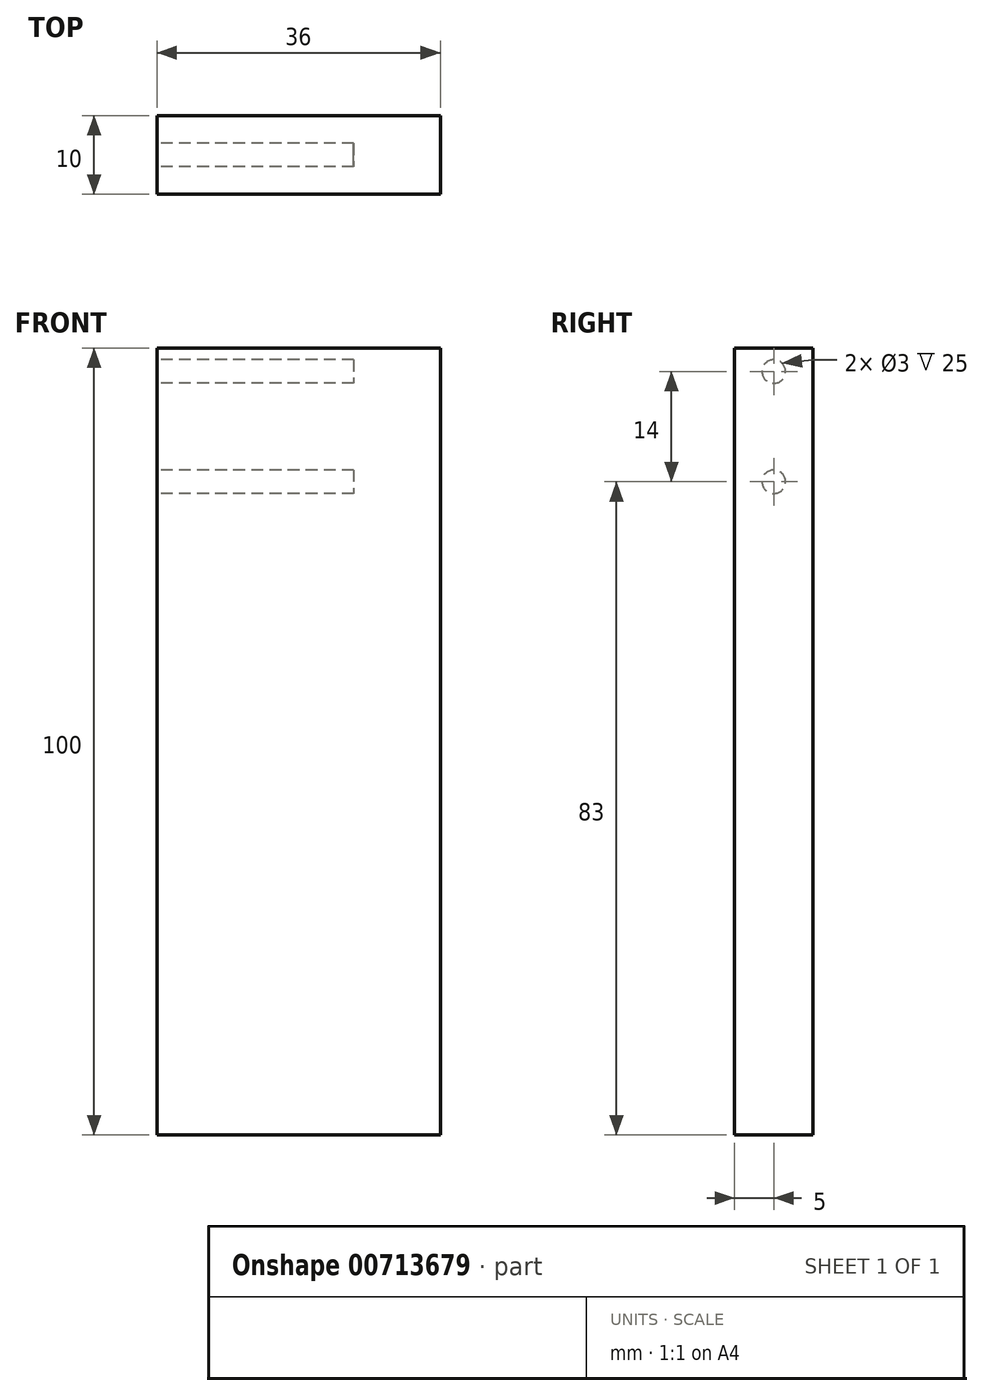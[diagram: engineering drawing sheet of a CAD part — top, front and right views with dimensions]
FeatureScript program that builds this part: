
annotation { "Feature Type Name" : "Feature", "Feature Type Description" : "" }
export const myFeature = defineFeature(function(context is Context, id is Id, definition is map)
    precondition{}
    {
        {
            var Q0;
            Q0=qCreatedBy(makeId("Front.planeOp"),FACE);
            var sketch = newSketch(context, id + "F0", { "sketchPlane" : qUnion([Q0])});
            skLineSegment(sketch, "E0.bottom", {"start": v(-18, 50) * mm, "end": v(18, 50) * mm});
            skLineSegment(sketch, "E0.top", {"start": v(-18, -50) * mm, "end": v(18, -50) * mm});
            skLineSegment(sketch, "E0.left", {"start": v(-18, 50) * mm, "end": v(-18, -50) * mm});
            skLineSegment(sketch, "E0.right", {"start": v(18, 50) * mm, "end": v(18, -50) * mm});
            skPoint(sketch, "E0.middle", {"position": v(0, 0) * mm});
            skSolve(sketch);
        }
        {
            var Q0;
            Q0=makeQuery(id+"F0.imprint","IMPRINT",FACE,{"disambiguationData":[TD([[makeQuery(id+"F0.imprint","IMPRINT",EDGE,{"derivedFrom":sQuery(id+"F0.wireOp",EDGE,"E0.bottom")}),-1.0]])]});
            extrude(context, id + "F1", {"entities" : qUnion([Q0]), "endBound" : BoundingType.SYMMETRIC, "depth" : 10 * mm, "offsetDistance" : 25 * mm});
        }
        {
            var Q0;
            Q0=makeQuery(id+"F1.opExtrude","SWEPT_FACE",FACE,{"disambiguationData":[OSD([sQuery(id+"F0.wireOp",EDGE,"E0.left")])]});
            var sketch = newSketch(context, id + "F2", { "sketchPlane" : qUnion([Q0])});
            skCircle(sketch, "E1", {"center": v(0, 47) * mm, "radius": 1.5 * mm});
            skCircle(sketch, "E2", {"center": v(0, 33) * mm, "radius": 1.5 * mm});
            skSolve(sketch);
        }
        {
            var Q0;
            Q0=makeQuery(id+"F2.imprint","IMPRINT",FACE,{"disambiguationData":[TD([[makeQuery(id+"F2.imprint","IMPRINT",EDGE,{"derivedFrom":sQuery(id+"F2.wireOp",EDGE,"E1")}),1.0]])]});
            var Q1;
            Q1=makeQuery(id+"F2.imprint","IMPRINT",FACE,{"disambiguationData":[TD([[makeQuery(id+"F2.imprint","IMPRINT",EDGE,{"derivedFrom":sQuery(id+"F2.wireOp",EDGE,"E2")}),1.0]])]});
            extrude(context, id + "F3", {"entities" : qUnion([Q0, Q1]), "operationType" : NewBodyOperationType.REMOVE, "oppositeDirection" : true, "depth" : 25 * mm, "offsetDistance" : 25 * mm});
        }
    });
